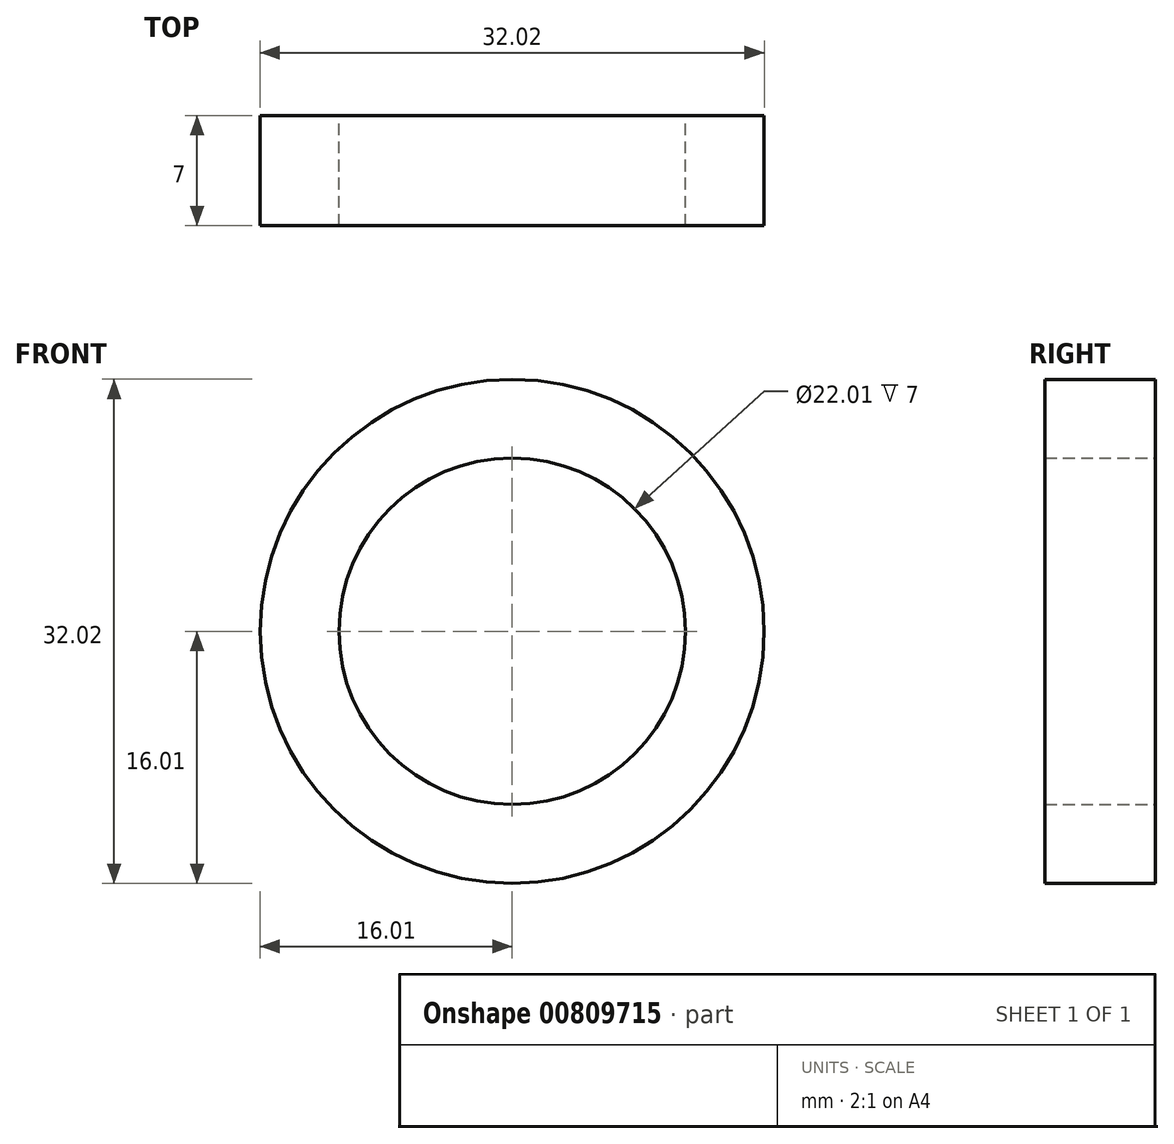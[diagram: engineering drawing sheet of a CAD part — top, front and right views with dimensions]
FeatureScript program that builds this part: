
annotation { "Feature Type Name" : "Feature", "Feature Type Description" : "" }
export const myFeature = defineFeature(function(context is Context, id is Id, definition is map)
    precondition{}
    {
        {
            var Q0;
            Q0=qCreatedBy(makeId("Front.planeOp"),FACE);
            var sketch = newSketch(context, id + "F0", { "sketchPlane" : qUnion([Q0])});
            skCircle(sketch, "E0", {"center": v(0, 0) * mm, "radius": 11 * mm});
            skCircle(sketch, "E1", {"center": v(0, 0) * mm, "radius": 16 * mm});
            skSolve(sketch);
        }
        {
            var Q0;
            Q0=makeQuery(id+"F0.imprint","IMPRINT",FACE,{"disambiguationData":[TD([[makeQuery(id+"F0.imprint","IMPRINT",EDGE,{"derivedFrom":sQuery(id+"F0.wireOp",EDGE,"E0")}),-1.0]])]});
            extrude(context, id + "F1", {"entities" : qUnion([Q0]), "depth" : 7 * mm, "offsetDistance" : 25 * mm});
        }
    });
